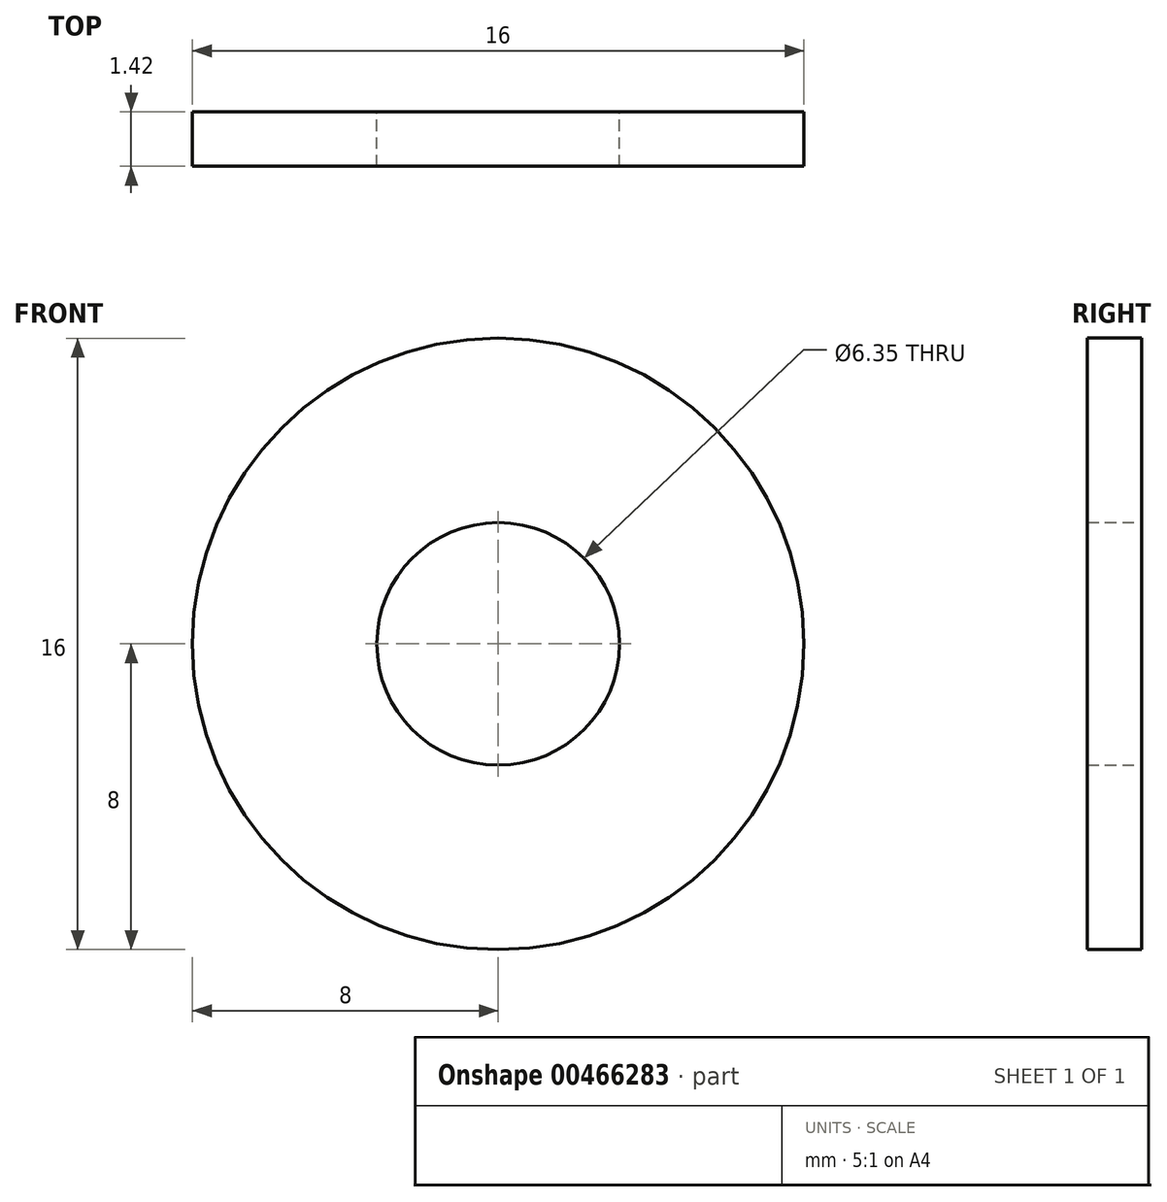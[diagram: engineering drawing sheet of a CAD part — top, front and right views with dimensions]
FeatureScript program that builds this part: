
annotation { "Feature Type Name" : "Feature", "Feature Type Description" : "" }
export const myFeature = defineFeature(function(context is Context, id is Id, definition is map)
    precondition{}
    {
        {
            var Q0;
            Q0=qCreatedBy(makeId("Front.planeOp"),FACE);
            var sketch = newSketch(context, id + "F0", { "sketchPlane" : qUnion([Q0])});
            skCircle(sketch, "E0", {"center": v(0, 0) * mm, "radius": 3.18 * mm});
            skCircle(sketch, "E1", {"center": v(0, 0) * mm, "radius": 8 * mm});
            skSolve(sketch);
        }
        {
            var Q0;
            Q0=makeQuery(id+"F0.imprint","IMPRINT",FACE,{"disambiguationData":[TD([[makeQuery(id+"F0.imprint","IMPRINT",EDGE,{"derivedFrom":sQuery(id+"F0.wireOp",EDGE,"E0")}),-1.0]])]});
            extrude(context, id + "F1", {"entities" : qUnion([Q0]), "depth" : 1.42 * mm, "offsetDistance" : 25.4 * mm});
        }
    });
